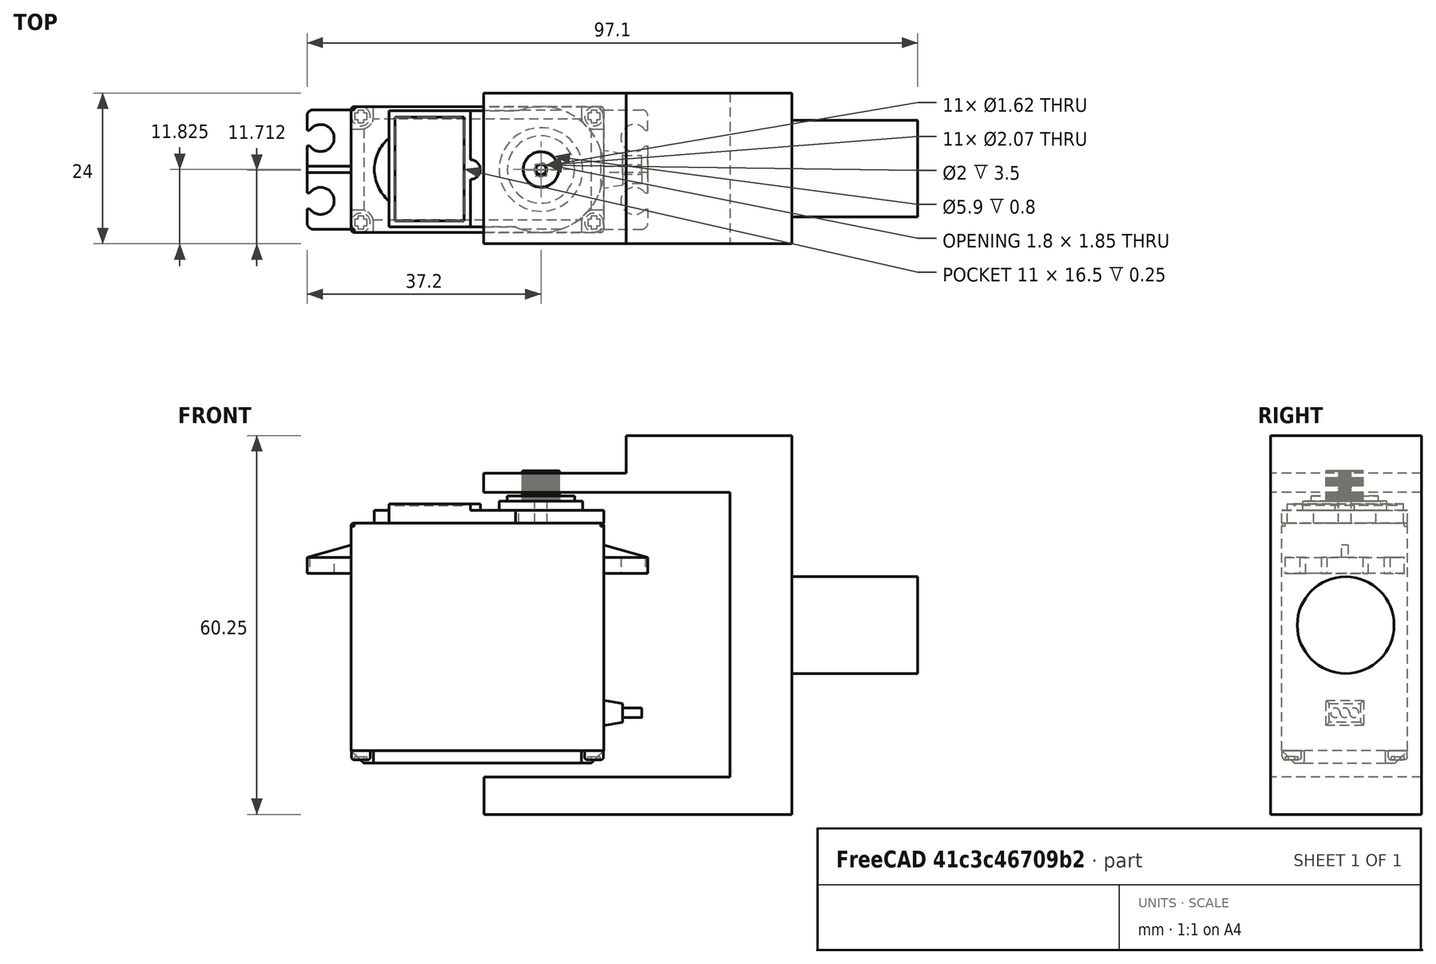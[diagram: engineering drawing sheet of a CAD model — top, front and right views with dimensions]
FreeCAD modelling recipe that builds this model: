
FCSTD DOCUMENT  (FreeCAD 0.21R33771 (Git))
Label: U_Servo_angulo_v2
License: All rights reserved
LicenseURL: http://en.wikipedia.org/wiki/All_rights_reserved
objects: Sketcher::SketchObject×2, PartDesign::Pad×2, Mesh::Feature×1, Part::Feature×1, PartDesign::Body×1
note: 8 computed .brp shape members not serialized (recipe doc carries the construction recipe); baked Part::Feature solids carry a one-line shape summary decoded from their .brp

FEATURE [Mesh::Feature] servo_lower_cover_fake_shaft
  Placement = pos=(0,-12,2) rot=(0,1,0;3.14159rad)
FEATURE [Part::Feature] Part__Feature  label="MG996R"
  Placement = pos=(0,-9,-0.5) rot=(0,0,1;0rad)
  shape: bbox 54.21 x 20.13 x 46.64 mm, 453 faces, 11 solids (baked)
FEATURE [Sketcher::SketchObject] Sketch
  FullyConstrained = false
  MapMode = 5
  Placement = pos=(0,0,0) rot=(1,0,0;1.5708rad)
  Support = -> [XZ_Plane]
  sketch-geometry (10):
    g0: LineSegment StartX=1.01714 StartY=-4.08621 StartZ=0 EndX=40.1359 EndY=-4.08621 EndZ=0
    g1: LineSegment StartX=1.01714 StartY=-10.0633 StartZ=0 EndX=50 EndY=-10.0633 EndZ=0
    g2: LineSegment StartX=40.1359 StartY=-4.08621 StartZ=0 EndX=40.1359 EndY=41.1434 EndZ=0
    g3: LineSegment StartX=40.1359 StartY=41.1434 StartZ=0 EndX=1.00976 EndY=41.1434 EndZ=0
    g4: LineSegment StartX=1.00976 StartY=44.2323 StartZ=0 EndX=23.6784 EndY=44.2323 EndZ=0
    g5: LineSegment StartX=23.6784 StartY=50.1921 StartZ=0 EndX=50 EndY=50.1921 EndZ=0
    g6: LineSegment StartX=50 StartY=-10.0633 StartZ=0 EndX=50 EndY=50.1921 EndZ=0
    g7: LineSegment StartX=1.00976 StartY=44.2323 StartZ=0 EndX=1.00976 EndY=41.1434 EndZ=0
    g8: LineSegment StartX=23.6784 StartY=50.1921 StartZ=0 EndX=23.6784 EndY=44.2323 EndZ=0
    g9: LineSegment StartX=1.01714 StartY=-4.08621 StartZ=0 EndX=1.01714 EndY=-10.0633 EndZ=0
  constraints (20):
    c: Horizontal(g0)
    c: Horizontal(g1)
    c: Coincident(g2,g0)
    c: Vertical(g2)
    c: Coincident(g3,g2)
    c: Horizontal(g3)
    c: Horizontal(g4)
    c: Horizontal(g5)
    c: Coincident(g6,g1)
    c: Coincident(g6,g5)
    c: Vertical(g6)
    c: Coincident(g7,g4)
    c: Coincident(g7,g3)
    c: Vertical(g7)
    c: Coincident(g8,g5)
    c: Coincident(g8,g4)
    c: Vertical(g8)
    c: Coincident(g9,g0)
    c: Coincident(g9,g1)
    c: Vertical(g9)
FEATURE [PartDesign::Pad] Pad
  Direction = (0,-1,2e-16)
  Length = 24
  Length2 = 10
  Placement = pos=(0,0,0) rot=(1,0,0;1.5708rad)
  Profile = -> Sketch
  ReferenceAxis = -> Sketch [N_Axis]
  Type = 0
FEATURE [Sketcher::SketchObject] Sketch001
  FullyConstrained = false
  MapMode = 5
  Placement = pos=(50,0,0) rot=(0.707107,0,0.707107;3.14159rad)
  Support = -> [Pad]
  sketch-geometry (1):
    g0: Circle CenterX=20.0454 CenterY=12.0314 CenterZ=0 NormalX=0 NormalY=0 NormalZ=1 AngleXU=0 Radius=7.70236
FEATURE [PartDesign::Pad] Pad001
  BaseFeature = -> Pad
  Direction = (1,0,-2e-16)
  Length = 20
  Length2 = 10
  Placement = pos=(0,0,0) rot=(1,0,0;1.5708rad)
  Profile = -> Sketch001
  ReferenceAxis = -> Sketch001 [N_Axis]
  Type = 0
FEATURE [PartDesign::Body] Body  label="U_redondo"
  Group = -> [Sketch,Pad,Sketch001,Pad001]
  Origin = -> Origin
  Tip = -> Pad001
